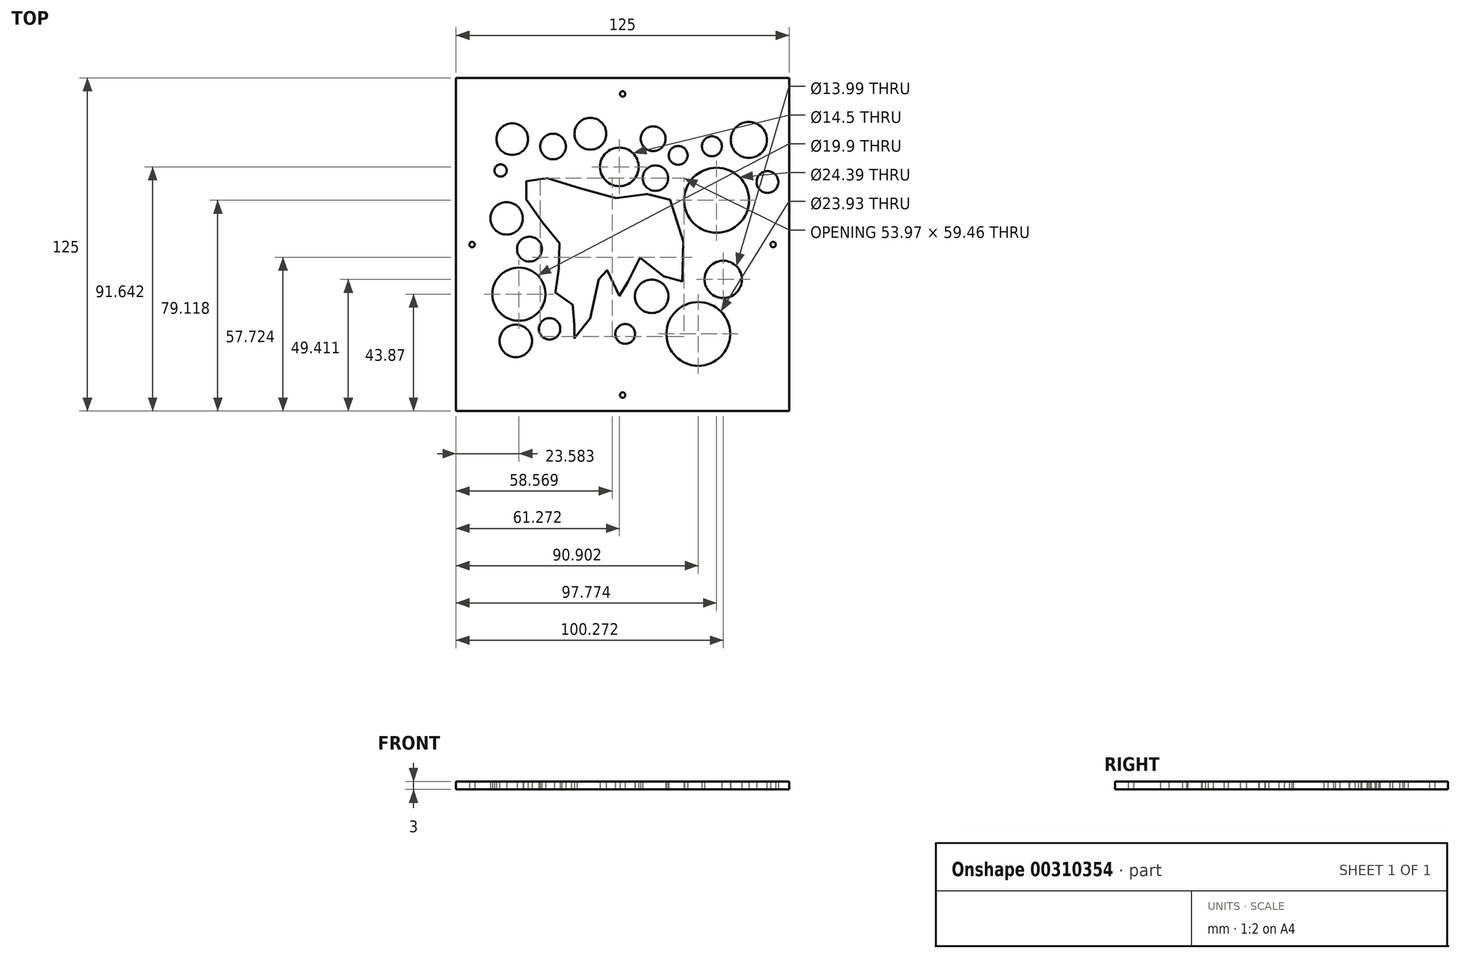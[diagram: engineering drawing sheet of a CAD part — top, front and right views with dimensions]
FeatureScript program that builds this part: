
annotation { "Feature Type Name" : "Feature", "Feature Type Description" : "" }
export const myFeature = defineFeature(function(context is Context, id is Id, definition is map)
    precondition{}
    {
        {
            var Q0;
            Q0=qCreatedBy(makeId("Top.planeOp"),FACE);
            var sketch = newSketch(context, id + "F0", { "sketchPlane" : qUnion([Q0])});
            skLineSegment(sketch, "E0.bottom", {"start": v(-95.34, -63.45) * mm, "end": v(29.66, -63.45) * mm});
            skLineSegment(sketch, "E0.top", {"start": v(-95.34, 61.55) * mm, "end": v(29.66, 61.55) * mm});
            skLineSegment(sketch, "E0.left", {"start": v(-95.34, -63.45) * mm, "end": v(-95.34, 61.55) * mm});
            skLineSegment(sketch, "E0.right", {"start": v(29.66, -63.45) * mm, "end": v(29.66, 61.55) * mm});
            skCircle(sketch, "E1", {"center": v(23.66, -0.95) * mm, "radius": 1 * mm});
            skCircle(sketch, "E2", {"center": v(-32.84, -57.45) * mm, "radius": 1 * mm});
            skCircle(sketch, "E3", {"center": v(-89.34, -0.95) * mm, "radius": 1 * mm});
            skCircle(sketch, "E4", {"center": v(-32.84, 55.55) * mm, "radius": 1 * mm});
            skCircle(sketch, "E5", {"center": v(-4.44, -34.5) * mm, "radius": 11.97 * mm});
            skCircle(sketch, "E6", {"center": v(2.43, 15.67) * mm, "radius": 12.2 * mm});
            skCircle(sketch, "E7", {"center": v(-71.76, -19.58) * mm, "radius": 9.95 * mm});
            skCircle(sketch, "E8", {"center": v(-44.95, 40.62) * mm, "radius": 5.97 * mm});
            skCircle(sketch, "E9", {"center": v(-34.07, 28.2) * mm, "radius": 7.25 * mm});
            skCircle(sketch, "E10", {"center": v(-20.53, 23.95) * mm, "radius": 4.78 * mm});
            skCircle(sketch, "E11", {"center": v(-58.96, 35.84) * mm, "radius": 4.8 * mm});
            skCircle(sketch, "E12", {"center": v(-76.38, 8.86) * mm, "radius": 6.07 * mm});
            skCircle(sketch, "E13", {"center": v(4.93, -14.04) * mm, "radius": 7 * mm});
            skCircle(sketch, "E14", {"center": v(-31.87, -34.5) * mm, "radius": 3.72 * mm});
            skCircle(sketch, "E15", {"center": v(-60.25, -32.6) * mm, "radius": 4.02 * mm});
            skCircle(sketch, "E16", {"center": v(-67.8, -2.68) * mm, "radius": 4.66 * mm});
            skCircle(sketch, "E17", {"center": v(0.68, 35.92) * mm, "radius": 3.74 * mm});
            skCircle(sketch, "E18", {"center": v(21.53, 22.51) * mm, "radius": 4.08 * mm});
            skCircle(sketch, "E19", {"center": v(-21.92, -20.39) * mm, "radius": 6.28 * mm});
            skCircle(sketch, "E20", {"center": v(-72.95, -37.11) * mm, "radius": 6.1 * mm});
            skCircle(sketch, "E21", {"center": v(-78.64, 26.84) * mm, "radius": 2.3 * mm});
            skFitSpline(sketch, "E22", {"points": [v(-61.15, 24) * mm, v(-69.8, 21.62) * mm, v(-64.73, 9.4) * mm, v(-55.64, -4) * mm, v(-58.02, -19.05) * mm, v(-50.13, -25.46) * mm, v(-52.06, -35.59) * mm, v(-46.25, -31.71) * mm, v(-39.7, -9.37) * mm, v(-33, -20.99) * mm, v(-26.89, -5.94) * mm, v(-11.99, -16.37) * mm, v(-15.41, 16.26) * mm, v(-31.95, 16.4) * mm, v(-61.15, 24) * mm]});
            skCircle(sketch, "E23", {"center": v(-56.83, 8.66) * mm, "radius": 3.62 * mm});
            skCircle(sketch, "E24", {"center": v(-51.32, 14.77) * mm, "radius": 4 * mm});
            skCircle(sketch, "E25", {"center": v(14.53, 38.3) * mm, "radius": 6.78 * mm});
            skCircle(sketch, "E26", {"center": v(-21.37, 38.75) * mm, "radius": 4.66 * mm});
            skCircle(sketch, "E27", {"center": v(-11.99, 32.5) * mm, "radius": 3.53 * mm});
            skCircle(sketch, "E28", {"center": v(-74.26, 38.6) * mm, "radius": 5.93 * mm});
            skSolve(sketch);
        }
        {
            var Q0;
            Q0=makeQuery(id+"F0.imprint","IMPRINT",FACE,{"disambiguationData":[TD([[makeQuery(id+"F0.imprint","IMPRINT",EDGE,{"derivedFrom":sQuery(id+"F0.wireOp",EDGE,"E0.bottom")}),1.0]])]});
            extrude(context, id + "F1", {"entities" : qUnion([Q0]), "depth" : 3 * mm});
        }
    });
